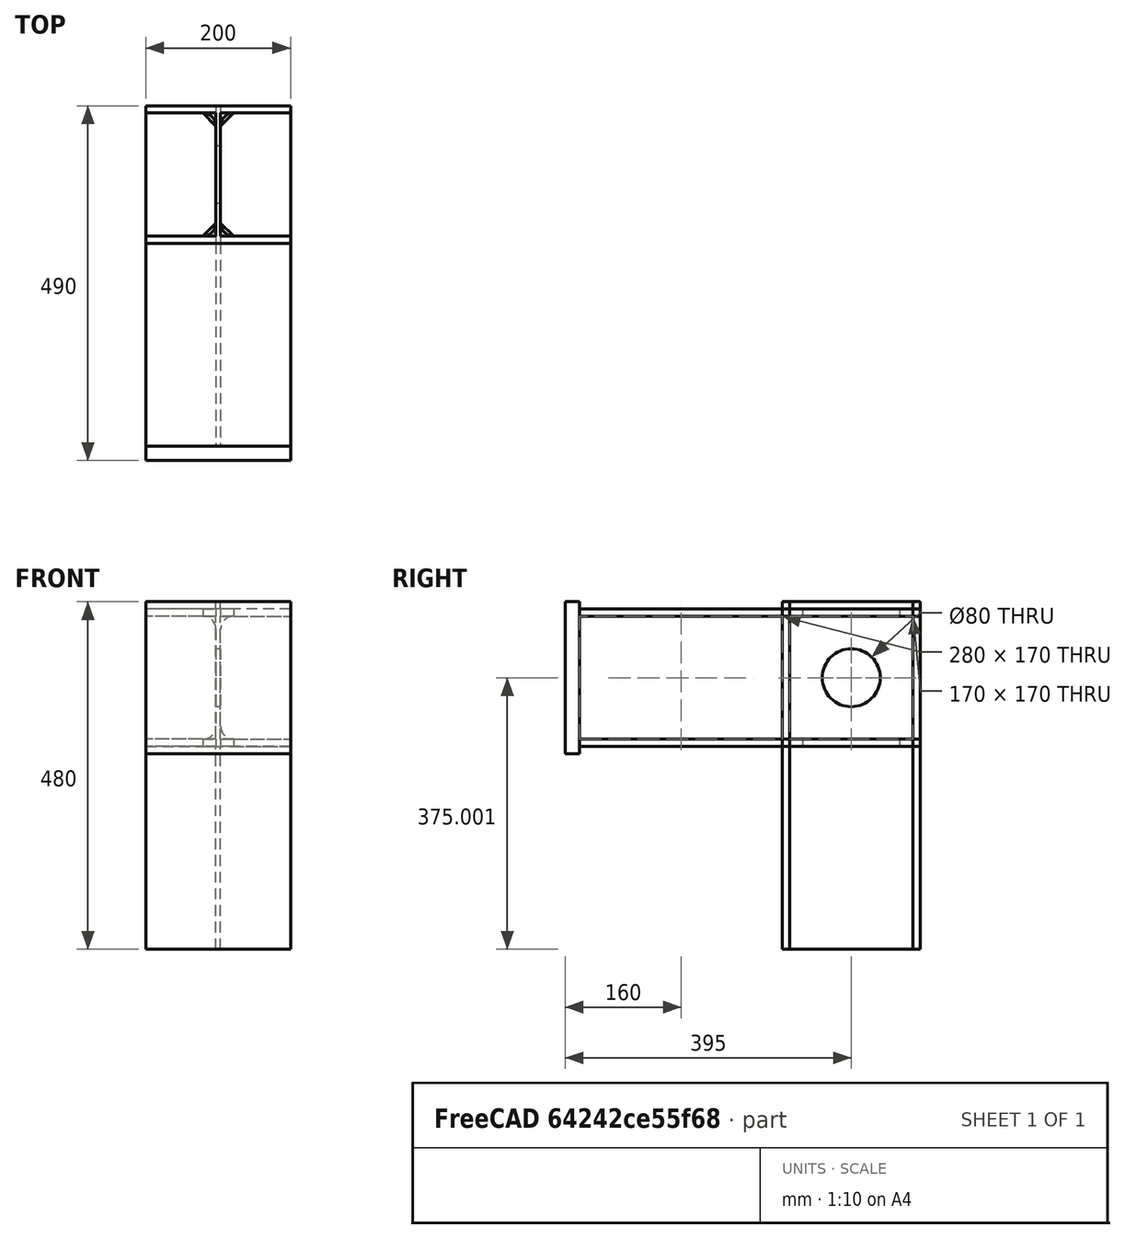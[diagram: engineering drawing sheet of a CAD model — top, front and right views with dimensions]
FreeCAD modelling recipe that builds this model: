
FCSTD DOCUMENT  (FreeCAD 0.21R33694 (Git))
Label: HEA200_frame_corner
License: All rights reserved
LicenseURL: http://en.wikipedia.org/wiki/All_rights_reserved
objects: Sketcher::SketchObject×4, Part::Extrusion×4, Fem::ConstraintForce×2, Part::Feature×1, Part::MultiFuse×1, App::MaterialObjectPython×1, Fem::ConstraintFixed×1, Fem::FemSolverObjectPython×1, Part::FeaturePython×1, Part::Cut×1, Fem::FeaturePython×1, Fem::FemMeshObjectPython×1, Fem::FemAnalysis×1
note: 12 computed .brp shape members not serialized (recipe doc carries the construction recipe); baked Part::Feature solids carry a one-line shape summary decoded from their .brp

FEATURE [Part::Feature] Fusion003012  label="corner"
  shape: bbox 200 x 470 x 480 mm, 60 faces (baked)
FEATURE [Sketcher::SketchObject] Sketch
  ExternalGeometry = -> [Fusion003012]
  FullyConstrained = true
  MapMode = 5
  Placement = pos=(0,5070,0) rot=(1,0,0;1.5708rad)
  Support = -> [Fusion003012]
  sketch-geometry (4):
    g0: LineSegment StartX=336.75 StartY=7245.73 StartZ=0 EndX=536.75 EndY=7245.73 EndZ=0
    g1: LineSegment StartX=536.75 StartY=7245.73 StartZ=0 EndX=536.75 EndY=7035.73 EndZ=0
    g2: LineSegment StartX=536.75 StartY=7035.73 StartZ=0 EndX=336.75 EndY=7035.73 EndZ=0
    g3: LineSegment StartX=336.75 StartY=7035.73 StartZ=0 EndX=336.75 EndY=7245.73 EndZ=0
  constraints (12):
    c: Coincident(g0,g1)
    c: Coincident(g1,g2)
    c: Coincident(g2,g3)
    c: Coincident(g3,g0)
    c: Horizontal(g0)
    c: Horizontal(g2)
    c: Vertical(g1)
    c: Vertical(g3)
    c: Vertical(g0,g-3)
    c: Vertical(g-3,g0)
    c: DistanceY(g-3,g0) = 10
    c: DistanceY(g1,g-4) = 10
FEATURE [Part::Extrusion] Extrude
  Base = -> Sketch
  Dir = (0,-1,2e-16)
  DirMode = 2
  FaceMakerClass = Part::FaceMakerBullseye
  LengthFwd = 20
  LengthRev = 0
  Solid = true
  Symmetric = false
FEATURE [Part::MultiFuse] Fusion
  Refine = true
  Shapes = -> [Fusion003012,Extrude]
FEATURE [App::MaterialObjectPython] MaterialSolid  label="S235"  # material (typed FeaturePython)
  Category = 0
  Material = AuthorAndLicense=(c) 2013 Juergen Riegel (CC-BY 3.0),CardName=CalculiX-Steel,Density=7900 kg/m^3,+8 more (map truncated)
FEATURE [Fem::ConstraintFixed] ConstraintFixed
  NormalDirection = (0,0,-1)
  Normals = (8) [(0,0,-1),(0,0,-1),(0,0,-1),(0,0,-1),(0,0,-1),(0,0,-1),(0,0,-1),(0,0,-1)]
  Points = (8) [(336.75,5350,6765.73),(403.417,5350,6765.73),(470.084,5350,6765.73),(536.75,5350,6765.73),(336.75,5540,6765.73),(403.417,5540,6765.73),+2 more]
  References = -> [Fusion]
  Scale = 15
FEATURE [Fem::ConstraintForce] ConstraintForce
  Direction = -> Fusion [Edge39]
  DirectionVector = (0,-1,0)
  Force = 119000
  NormalDirection = (0,2e-16,1)
  Points = (12) [(336.75,5050,7245.73),(403.417,5050,7245.73),(470.084,5050,7245.73),(536.75,5050,7245.73),(336.75,5060,7245.73),(403.417,5060,7245.73),+6 more]
  References = -> [Fusion]
  Scale = 10
FEATURE [Fem::ConstraintForce] ConstraintForce001
  Direction = -> Fusion [Edge43]
  DirectionVector = (0,1,0)
  Force = 119000
  NormalDirection = (0,-2e-16,-1)
  Points = (12) [(536.75,5050,7035.73),(470.084,5050,7035.73),(403.417,5050,7035.73),(336.75,5050,7035.73),(536.75,5060,7035.73),(470.084,5060,7035.73),+6 more]
  References = -> [Fusion]
  Reversed = true
  Scale = 10
FEATURE [Fem::FemSolverObjectPython] SolverCcxTools  # FEM object (typed FeaturePython)
  AnalysisType = 0
  BeamShellResultOutput3D = true
  BucklingFactors = 1
  EigenmodeHighLimit = 1000000
  EigenmodeLowLimit = 0
  EigenmodesCount = 10
  GeometricalNonlinearity = 0
  IterationsControlParameterCutb = 0.25,0.5,0.75,0.85,,,1.5,
  IterationsControlParameterIter = 4,8,9,200,10,400,,200,,
  IterationsControlParameterTimeUse = false
  IterationsThermoMechMaximum = 2000
  IterationsUserDefinedIncrementations = false
  IterationsUserDefinedTimeStepLength = false
  MaterialNonlinearity = 0
  MatrixSolverType = 1
  SplitInputWriter = true
  ThermoMechSteadyState = true
  TimeEnd = 1
  TimeInitialStep = 0.01
FEATURE [Sketcher::SketchObject] Sketch001
  ExternalGeometry = -> [Fusion003012]
  FullyConstrained = true
  MapMode = 5
  Placement = pos=(0,5070,0) rot=(1,0,0;1.5708rad)
  Support = -> [Fusion003012]
  sketch-geometry (12):
    g0: LineSegment StartX=336.75 StartY=7235.73 StartZ=0 EndX=536.75 EndY=7235.73 EndZ=0
    g1: LineSegment StartX=536.75 StartY=7235.73 StartZ=0 EndX=536.75 EndY=7225.73 EndZ=0
    g2: LineSegment StartX=536.75 StartY=7225.73 StartZ=0 EndX=440 EndY=7225.73 EndZ=0
    g3: LineSegment StartX=440 StartY=7055.73 StartZ=0 EndX=440 EndY=7225.73 EndZ=0
    g4: LineSegment StartX=336.75 StartY=7225.73 StartZ=0 EndX=433.5 EndY=7225.73 EndZ=0
    g5: LineSegment StartX=536.75 StartY=7055.73 StartZ=0 EndX=440 EndY=7055.73 EndZ=0
    g6: LineSegment StartX=433.5 StartY=7225.73 StartZ=0 EndX=433.5 EndY=7055.73 EndZ=0
    g7: LineSegment StartX=336.75 StartY=7055.73 StartZ=0 EndX=433.5 EndY=7055.73 EndZ=0
    g8: LineSegment StartX=336.75 StartY=7235.73 StartZ=0 EndX=336.75 EndY=7225.73 EndZ=0
    g9: LineSegment StartX=336.75 StartY=7055.73 StartZ=0 EndX=336.75 EndY=7045.73 EndZ=0
    g10: LineSegment StartX=536.75 StartY=7055.73 StartZ=0 EndX=536.75 EndY=7045.73 EndZ=0
    g11: LineSegment StartX=336.75 StartY=7045.73 StartZ=0 EndX=536.75 EndY=7045.73 EndZ=0
  constraints (29):
    c: Coincident(g0,g-3)
    c: Coincident(g1,g0)
    c: Coincident(g1,g-8)
    c: Vertical(g1)
    c: Coincident(g2,g1)
    c: Horizontal(g2)
    c: Vertical(g3)
    c: Coincident(g3,g2)
    c: Coincident(g4,g-7)
    c: Horizontal(g4)
    c: Coincident(g5,g-6)
    c: Horizontal(g5)
    c: Coincident(g3,g5)
    c: Coincident(g6,g4)
    c: Vertical(g6)
    c: Coincident(g7,g-5)
    c: Coincident(g8,g0)
    c: Coincident(g8,g4)
    c: Coincident(g9,g7)
    c: Coincident(g9,g-4)
    c: Coincident(g10,g5)
    c: Coincident(g10,g-4)
    c: Horizontal(g7)
    c: Coincident(g7,g6)
    c: DistanceX(g6,g-9) = 0
    c: DistanceX(g-10,g3) = 0
    c: Horizontal(g0)
    c: Coincident(g11,g9)
    c: Coincident(g11,g10)
FEATURE [Sketcher::SketchObject] Sketch002
  ExternalGeometry = -> [Fusion003012]
  FullyConstrained = true
  MapMode = 5
  Placement = pos=(0,0,7245.73) rot=(0,0,1;0rad)
  Support = -> [Fusion003012]
  sketch-geometry (12):
    g0: LineSegment StartX=336.75 StartY=5540 StartZ=0 EndX=536.75 EndY=5540 EndZ=0
    g1: LineSegment StartX=536.75 StartY=5540 StartZ=0 EndX=536.75 EndY=5530 EndZ=0
    g2: LineSegment StartX=336.75 StartY=5540 StartZ=0 EndX=336.75 EndY=5530 EndZ=0
    g3: LineSegment StartX=336.75 StartY=5530 StartZ=0 EndX=433.5 EndY=5530 EndZ=0
    g4: LineSegment StartX=440 StartY=5530 StartZ=0 EndX=536.75 EndY=5530 EndZ=0
    g5: LineSegment StartX=433.5 StartY=5530 StartZ=0 EndX=433.5 EndY=5360 EndZ=0
    g6: LineSegment StartX=440 StartY=5530 StartZ=0 EndX=440 EndY=5360 EndZ=0
    g7: LineSegment StartX=336.75 StartY=5360 StartZ=0 EndX=433.5 EndY=5360 EndZ=0
    g8: LineSegment StartX=440 StartY=5360 StartZ=0 EndX=536.75 EndY=5360 EndZ=0
    g9: LineSegment StartX=336.75 StartY=5360 StartZ=0 EndX=336.75 EndY=5350 EndZ=0
    g10: LineSegment StartX=336.75 StartY=5350 StartZ=0 EndX=536.75 EndY=5350 EndZ=0
    g11: LineSegment StartX=536.75 StartY=5350 StartZ=0 EndX=536.75 EndY=5360 EndZ=0
  constraints (28):
    c: Coincident(g0,g-3)
    c: Coincident(g0,g-3)
    c: Coincident(g1,g0)
    c: Coincident(g1,g-5)
    c: Coincident(g2,g0)
    c: Coincident(g2,g-4)
    c: Coincident(g3,g2)
    c: Horizontal(g3)
    c: Coincident(g4,g1)
    c: Horizontal(g4)
    c: Coincident(g5,g3)
    c: Vertical(g5)
    c: Coincident(g6,g4)
    c: Vertical(g6)
    c: Coincident(g7,g-8)
    c: Horizontal(g7)
    c: Coincident(g5,g7)
    c: Coincident(g6,g8)
    c: Coincident(g8,g-9)
    c: Coincident(g9,g7)
    c: Coincident(g9,g-10)
    c: Coincident(g10,g9)
    c: Coincident(g10,g-10)
    c: Coincident(g11,g10)
    c: Coincident(g11,g8)
    c: Horizontal(g8)
    c: DistanceX(g-7,g6) = 0
    c: DistanceX(g5,g-6) = 0
FEATURE [Part::Extrusion] Extrude002
  Base = -> Sketch002
  Dir = (0,0,1)
  DirMode = 2
  FaceMakerClass = Part::FaceMakerBullseye
  LengthFwd = 0
  LengthRev = 480
  Solid = true
  Symmetric = false
FEATURE [Part::Extrusion] Extrude001
  Base = -> Sketch001
  Dir = (0,-1,2e-16)
  DirMode = 2
  FaceMakerClass = Part::FaceMakerBullseye
  LengthFwd = 0
  LengthRev = 470
  Solid = true
  Symmetric = false
FEATURE [Part::FeaturePython] BooleanFragments  # WARN: FeaturePython — macro-defined, semantics opaque (R4)
  Mode = 2
  Objects = -> [Extrude,Extrude001,Extrude002]
  Tolerance = 0
FEATURE [Sketcher::SketchObject] Sketch003
  ExternalGeometry = -> [BooleanFragments]
  FullyConstrained = true
  MapMode = 5
  Placement = pos=(536.75,0,0) rot=(0.57735,0.57735,0.57735;2.0944rad)
  Support = -> [BooleanFragments]
  sketch-geometry (1):
    g0: Circle CenterX=5445 CenterY=7140.73 CenterZ=0 NormalX=0 NormalY=0 NormalZ=1 AngleXU=0 Radius=40
  constraints (3):
    c: DistanceX(g-3,g0) = 85
    c: DistanceY(g-3,g0) = 85
    c: Diameter(g0) = 80
FEATURE [Part::Extrusion] Extrude004
  Base = -> Sketch003
  Dir = (1,0,0)
  DirMode = 2
  FaceMakerClass = Part::FaceMakerBullseye
  LengthFwd = 0
  LengthRev = 200
  Solid = true
  Symmetric = false
FEATURE [Part::Cut] Cut
  Base = -> BooleanFragments
  Tool = -> Extrude004
FEATURE [Fem::FeaturePython] MeshRegion  # FEM object (typed FeaturePython)
  CharacteristicLength = 25
  References = -> [Cut]
FEATURE [Fem::FemMeshObjectPython] FEMMeshGmsh  # FEM object (typed FeaturePython)
  Algorithm2D = 0
  Algorithm3D = 0
  CharacteristicLengthMax = 50
  CharacteristicLengthMin = 0
  CoherenceMesh = true
  ElementDimension = 0
  ElementOrder = 1
  GeometryTolerance = 1e-06
  GroupsOfNodes = false
  HighOrderOptimize = 0
  MeshRegionList = -> [MeshRegion]
  MeshSizeFromCurvature = 12
  OptimizeNetgen = false
  OptimizeStd = true
  Part = -> Cut
  RecombinationAlgorithm = 0
  Recombine3DAll = false
  RecombineAll = false
  SecondOrderLinear = false
FEATURE [Fem::FemAnalysis] Analysis
  Group = -> [MaterialSolid,ConstraintFixed,ConstraintForce,ConstraintForce001,SolverCcxTools,FEMMeshGmsh]
